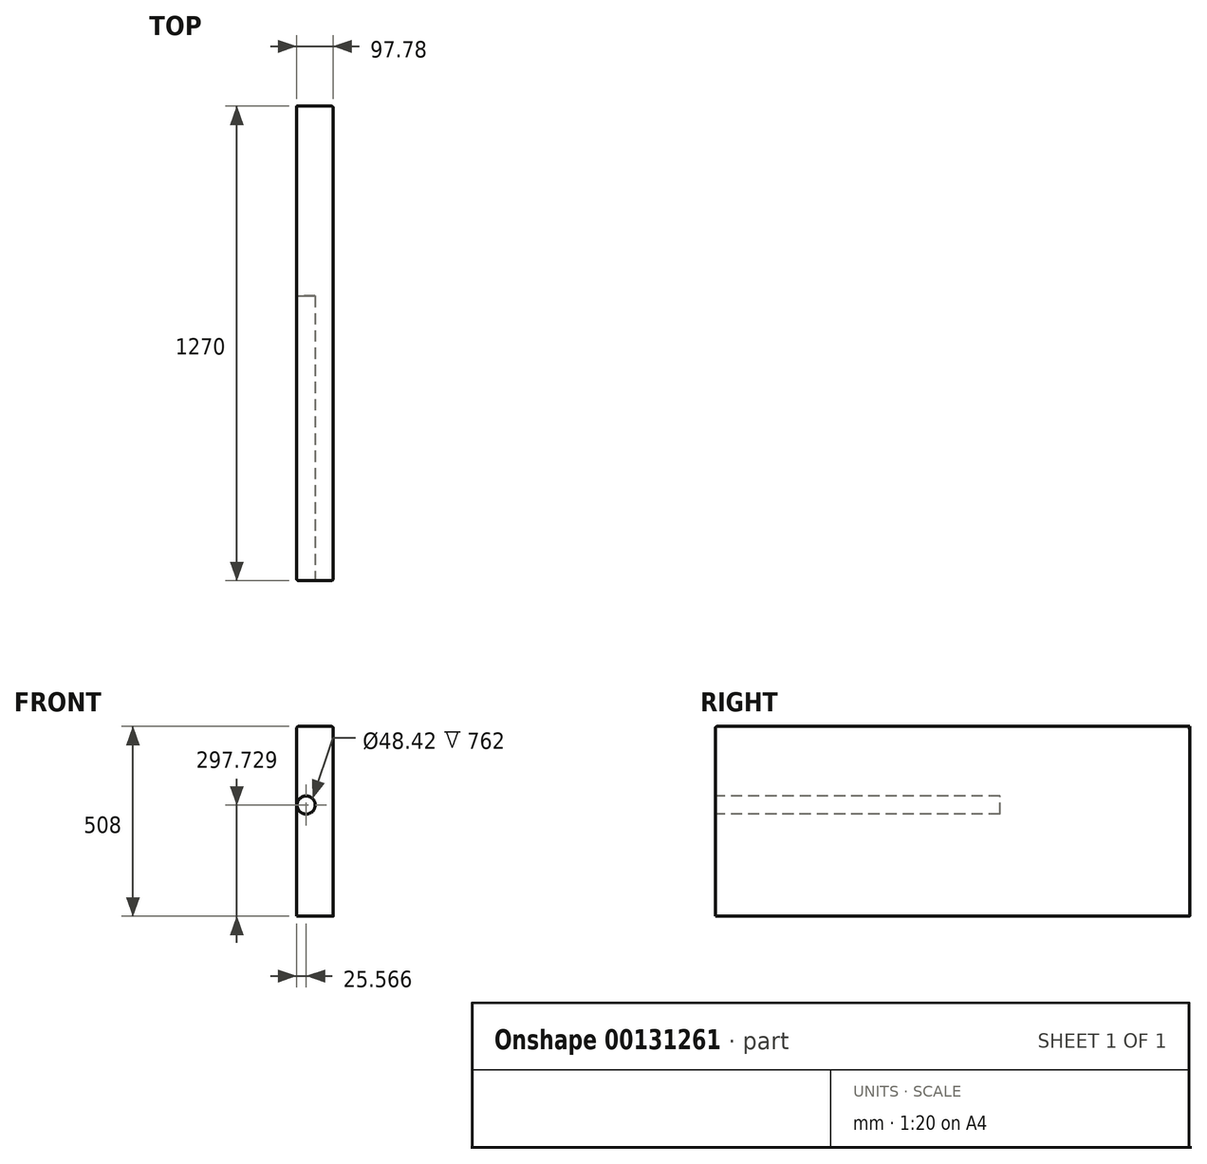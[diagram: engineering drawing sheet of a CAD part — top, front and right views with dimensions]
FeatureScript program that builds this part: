
annotation { "Feature Type Name" : "Feature", "Feature Type Description" : "" }
export const myFeature = defineFeature(function(context is Context, id is Id, definition is map)
    precondition{}
    {
        {
            var Q0;
            Q0=qCreatedBy(makeId("Top.planeOp"),FACE);
            var sketch = newSketch(context, id + "F0", { "sketchPlane" : qUnion([Q0])});
            skLineSegment(sketch, "E0.bottom", {"start": v(-50.19, 1241.15) * mm, "end": v(47.59, 1241.15) * mm});
            skLineSegment(sketch, "E0.top", {"start": v(-50.19, -28.85) * mm, "end": v(47.59, -28.85) * mm});
            skLineSegment(sketch, "E0.left", {"start": v(-50.19, 1241.15) * mm, "end": v(-50.19, -28.85) * mm});
            skLineSegment(sketch, "E0.right", {"start": v(47.59, 1241.15) * mm, "end": v(47.59, -28.85) * mm});
            skSolve(sketch);
        }
        {
            var Q0;
            Q0=makeQuery(id+"F0.imprint","IMPRINT",FACE,{"disambiguationData":[TD([[makeQuery(id+"F0.imprint","IMPRINT",EDGE,{"derivedFrom":sQuery(id+"F0.wireOp",EDGE,"E0.bottom")}),-1.0]])]});
            extrude(context, id + "F1", {"entities" : qUnion([Q0]), "depth" : 508 * mm});
        }
        {
            var Q0;
            Q0=makeQuery(id+"F1.opExtrude","SWEPT_FACE",FACE,{"disambiguationData":[OSD([sQuery(id+"F0.wireOp",EDGE,"E0.top")])]});
            var sketch = newSketch(context, id + "F2", { "sketchPlane" : qUnion([Q0])});
            skCircle(sketch, "E1", {"center": v(-24.62, 297.73) * mm, "radius": 24.21 * mm});
            skSolve(sketch);
        }
        {
            var Q0;
            Q0=makeQuery(id+"F2.imprint","IMPRINT",FACE,{"disambiguationData":[TD([[makeQuery(id+"F2.imprint","IMPRINT",EDGE,{"derivedFrom":sQuery(id+"F2.wireOp",EDGE,"E1")}),1.0]])]});
            extrude(context, id + "F3", {"entities" : qUnion([Q0]), "operationType" : NewBodyOperationType.REMOVE, "oppositeDirection" : true, "depth" : 762 * mm});
        }
        {
            var Q0;
            Q0=makeQuery(id+"F1.opExtrude","CAP_EDGE",EDGE,{"disambiguationData":[OSD([sQuery(id+"F0.wireOp",EDGE,"E0.top")])],"isStart":false});
            var Q1;
            Q1=makeQuery(id+"F1.opExtrude","CAP_EDGE",EDGE,{"disambiguationData":[OSD([sQuery(id+"F0.wireOp",EDGE,"E0.right")])],"isStart":false});
            var Q2;
            Q2=makeQuery(id+"F1.opExtrude","SWEPT_EDGE",EDGE,{"disambiguationData":[OSD([sQuery(id+"F0.wireOp",EDGE,"E0.top"),sQuery(id+"F0.wireOp",EDGE,"E0.right")])]});
            var Q3;
            Q3=makeQuery(id+"F1.opExtrude","SWEPT_EDGE",EDGE,{"disambiguationData":[OSD([sQuery(id+"F0.wireOp",EDGE,"E0.top"),sQuery(id+"F0.wireOp",EDGE,"E0.left")])]});
            var Q4;
            Q4=makeQuery(id+"F1.opExtrude","CAP_EDGE",EDGE,{"disambiguationData":[OSD([sQuery(id+"F0.wireOp",EDGE,"E0.left")])],"isStart":false});
            var Q5;
            Q5=makeQuery(id+"F1.opExtrude","SWEPT_EDGE",EDGE,{"disambiguationData":[OSD([sQuery(id+"F0.wireOp",EDGE,"E0.bottom"),sQuery(id+"F0.wireOp",EDGE,"E0.right")])]});
            fillet(context, id + "F4", {"entities" : qUnion([Q0, Q1, Q2, Q3, Q4, Q5]), "radius" : 5.08 * mm, "tangentPropagation" : true, "allowEdgeOverflow" : false});
        }
    });
